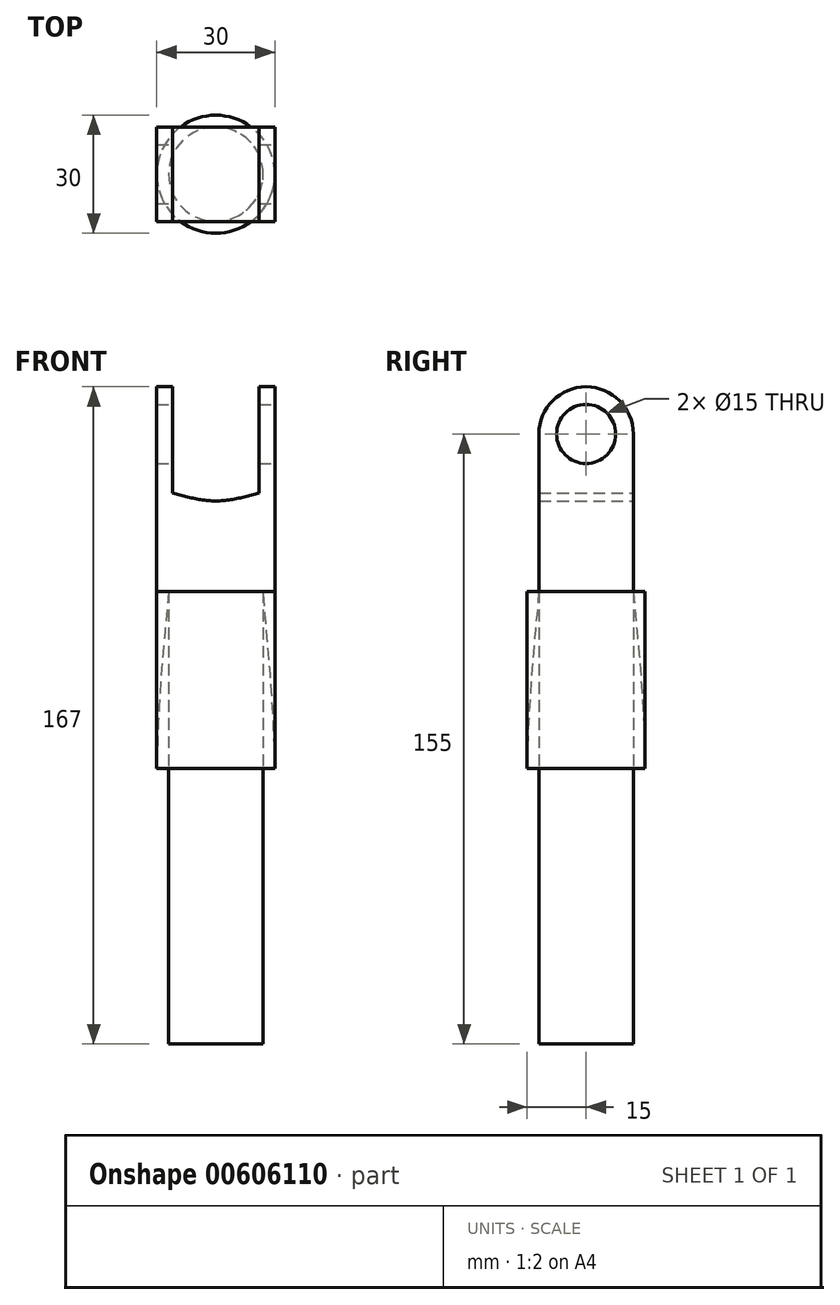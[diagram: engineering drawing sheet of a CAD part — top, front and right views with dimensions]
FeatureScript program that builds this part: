
annotation { "Feature Type Name" : "Feature", "Feature Type Description" : "" }
export const myFeature = defineFeature(function(context is Context, id is Id, definition is map)
    precondition{}
    {
        {
            var Q0;
            Q0=qCreatedBy(makeId("Top.planeOp"),FACE);
            var sketch = newSketch(context, id + "F0", { "sketchPlane" : qUnion([Q0])});
            skCircle(sketch, "E0", {"center": v(0, 0) * mm, "radius": 12 * mm});
            skSolve(sketch);
        }
        {
            var Q0;
            Q0=makeQuery(id+"F0.imprint","IMPRINT",FACE,{"disambiguationData":[TD([[makeQuery(id+"F0.imprint","IMPRINT",EDGE,{"derivedFrom":sQuery(id+"F0.wireOp",EDGE,"E0")}),1.0]])]});
            extrude(context, id + "F1", {"entities" : qUnion([Q0]), "endBound" : BoundingType.SYMMETRIC, "depth" : 30 * mm, "offsetDistance" : 25.4 * mm});
        }
        {
            var Q0;
            Q0=qCreatedBy(makeId("Right.planeOp"),FACE);
            var sketch = newSketch(context, id + "F2", { "sketchPlane" : qUnion([Q0])});
            skLineSegment(sketch, "E1.bottom", {"start": v(-15, 0) * mm, "end": v(15, 0) * mm});
            skLineSegment(sketch, "E1.top", {"start": v(-15, 100) * mm, "end": v(15, 100) * mm});
            skLineSegment(sketch, "E1.left", {"start": v(-15, 0) * mm, "end": v(-15, 100) * mm});
            skLineSegment(sketch, "E1.right", {"start": v(15, 0) * mm, "end": v(15, 100) * mm});
            skPoint(sketch, "E1.middle", {"position": v(0, 50) * mm});
            skLineSegment(sketch, "E2.bottom", {"start": v(-12, 100) * mm, "end": v(12, 100) * mm});
            skLineSegment(sketch, "E2.top", {"start": v(-12, 0) * mm, "end": v(12, 0) * mm});
            skLineSegment(sketch, "E2.left", {"start": v(-12, 100) * mm, "end": v(-12, 0) * mm});
            skLineSegment(sketch, "E2.right", {"start": v(12, 100) * mm, "end": v(12, 0) * mm});
            skFitSpline(sketch, "E3", {"points": [v(12, 100) * mm, v(15, 50) * mm, v(12, 15) * mm], "startDerivative": vector(8.76, -94.23) * mm, "endDerivative": vector(-9.56, -62.94) * mm});
            skLineSegment(sketch, "E4", {"start": v(0, 100) * mm, "end": v(0, 0) * mm, "construction": true});
            skLineSegment(sketch, "E5", {"start": v(12, 15) * mm, "end": v(0, 15) * mm});
            skLineSegment(sketch, "E6", {"start": v(0, 15) * mm, "end": v(0, 100) * mm});
            skSolve(sketch);
        }
        {
            var Q0;
            {var subQ5=sQuery(id+"F2.wireOp",EDGE,"E5");Q0=makeQuery(id+"F2.imprint","IMPRINT",FACE,{"disambiguationData":[TD([[makeQuery(id+"F2.imprint","IMPRINT",EDGE,{"derivedFrom":subQ5}),-1.0]])]});}
            var Q1;
            {var subQ0=sQuery(id+"F2.wireOp",EDGE,"E3");var subQ1=sQuery(id+"F2.wireOp",EDGE,"E1.right");var subQ2=makeQuery(id+"F2.imprint","INTERSECT",VERTEX,{"disambiguationData":[OD(0.0)],"derivedFrom":[subQ1,subQ0]});Q1=makeQuery(id+"F2.imprint","IMPRINT",FACE,{"disambiguationData":[TD([[makeQuery(id+"F2.imprint","IMPRINT",EDGE,{"disambiguationData":[TD([[subQ2,-1.0]])],"derivedFrom":subQ1}),1.0]])]});}
            var Q2;
            {var subQ0=sQuery(id+"F2.wireOp",EDGE,"E3");var subQ1=sQuery(id+"F2.wireOp",EDGE,"E1.right");var subQ2=makeQuery(id+"F2.imprint","INTERSECT",VERTEX,{"disambiguationData":[OD(0.0)],"derivedFrom":[subQ1,subQ0]});Q2=makeQuery(id+"F2.imprint","IMPRINT",FACE,{"disambiguationData":[TD([[makeQuery(id+"F2.imprint","IMPRINT",EDGE,{"disambiguationData":[TD([[subQ2,-1.0]])],"derivedFrom":subQ1}),-1.0]])]});}
            var Q3;
            Q3=sQuery(id+"F2.wireOp",EDGE,"E4");
            revolve(context, id + "F3", {"operationType" : NewBodyOperationType.ADD, "entities" : qUnion([Q0, Q1, Q2]), "axis" : qUnion([Q3]), "revolveType" : RevolveType.FULL});
        }
        {
            var Q0;
            Q0=qCreatedBy(makeId("Right.planeOp"),FACE);
            var sketch = newSketch(context, id + "F4", { "sketchPlane" : qUnion([Q0])});
            skLineSegment(sketch, "E7.bottom", {"start": v(12, 100) * mm, "end": v(-12, 100) * mm});
            skLineSegment(sketch, "E7.top", {"start": v(12, 140) * mm, "end": v(-12, 140) * mm});
            skLineSegment(sketch, "E7.left", {"start": v(12, 100) * mm, "end": v(12, 140) * mm});
            skLineSegment(sketch, "E7.right", {"start": v(-12, 100) * mm, "end": v(-12, 140) * mm});
            skPoint(sketch, "E7.middle", {"position": v(0, 120) * mm});
            skCircle(sketch, "E8", {"center": v(0, 140) * mm, "radius": 12 * mm});
            skCircle(sketch, "E9", {"center": v(0, 140) * mm, "radius": 7.5 * mm});
            skSolve(sketch);
        }
        {
            var Q0;
            Q0=makeQuery(id+"F4.imprint","IMPRINT",FACE,{"disambiguationData":[TD([[makeQuery(id+"F4.imprint","IMPRINT",EDGE,{"derivedFrom":sQuery(id+"F4.wireOp",EDGE,"E7.bottom")}),-1.0]])]});
            var Q1;
            {var subQ1=sQuery(id+"F4.wireOp",EDGE,"E7.top");var subQ3=sQuery(id+"F4.wireOp",EDGE,"E9");var subQ4=makeQuery(id+"F4.imprint","INTERSECT",VERTEX,{"disambiguationData":[OD(0.0)],"derivedFrom":[subQ1,subQ3]});Q1=makeQuery(id+"F4.imprint","IMPRINT",FACE,{"disambiguationData":[TD([[makeQuery(id+"F4.imprint","IMPRINT",EDGE,{"disambiguationData":[TD([[subQ4,1.0]])],"derivedFrom":subQ3}),-1.0]])]});}
            var Q2;
            {var subQ1=sQuery(id+"F4.wireOp",EDGE,"E7.top");var subQ3=sQuery(id+"F4.wireOp",EDGE,"E9");var subQ4=makeQuery(id+"F4.imprint","INTERSECT",VERTEX,{"disambiguationData":[OD(0.0)],"derivedFrom":[subQ1,subQ3]});Q2=makeQuery(id+"F4.imprint","IMPRINT",FACE,{"disambiguationData":[TD([[makeQuery(id+"F4.imprint","IMPRINT",EDGE,{"disambiguationData":[TD([[subQ4,-1.0]])],"derivedFrom":subQ3}),-1.0]])]});}
            extrude(context, id + "F5", {"entities" : qUnion([Q0, Q1, Q2]), "operationType" : NewBodyOperationType.ADD, "endBound" : BoundingType.SYMMETRIC, "oppositeDirection" : true, "depth" : 30 * mm, "offsetDistance" : 25.4 * mm});
        }
        {
            var Q0;
            Q0=makeQuery(id+"F5.opExtrude","SWEPT_FACE",FACE,{"disambiguationData":[OSD([sQuery(id+"F4.wireOp",EDGE,"E7.left")])]});
            var sketch = newSketch(context, id + "F6", { "sketchPlane" : qUnion([Q0])});
            skLineSegment(sketch, "E10.bottom", {"start": v(11, 155) * mm, "end": v(-11, 155) * mm});
            skLineSegment(sketch, "E10.top", {"start": v(11, 125) * mm, "end": v(-11, 125) * mm});
            skLineSegment(sketch, "E10.left", {"start": v(11, 155) * mm, "end": v(11, 125) * mm});
            skLineSegment(sketch, "E10.right", {"start": v(-11, 155) * mm, "end": v(-11, 125) * mm});
            skPoint(sketch, "E10.middle", {"position": v(0, 140) * mm});
            skLineSegment(sketch, "E11.bottom", {"start": v(11, 157) * mm, "end": v(-11, 157) * mm});
            skLineSegment(sketch, "E11.top", {"start": v(11, 123) * mm, "end": v(-11, 123) * mm});
            skLineSegment(sketch, "E11.left", {"start": v(11, 157) * mm, "end": v(11, 123) * mm});
            skLineSegment(sketch, "E11.right", {"start": v(-11, 157) * mm, "end": v(-11, 123) * mm});
            skFitSpline(sketch, "E12", {"points": [v(-11, 125) * mm, v(0, 123) * mm, v(11, 125) * mm], "startDerivative": vector(22, -6) * mm, "endDerivative": vector(22, 6) * mm});
            skSolve(sketch);
        }
        {
            var Q0;
            {var subQ0=sQuery(id+"F6.wireOp",EDGE,"E10.bottom");Q0=makeQuery(id+"F6.imprint","IMPRINT",FACE,{"disambiguationData":[TD([[makeQuery(id+"F6.imprint","IMPRINT",EDGE,{"derivedFrom":subQ0}),-1.0]])]});}
            var Q1;
            {var subQ0=sQuery(id+"F6.wireOp",EDGE,"E10.top");Q1=makeQuery(id+"F6.imprint","IMPRINT",FACE,{"disambiguationData":[TD([[makeQuery(id+"F6.imprint","IMPRINT",EDGE,{"derivedFrom":subQ0}),1.0]])]});}
            var Q2;
            {var subQ0=sQuery(id+"F6.wireOp",EDGE,"E10.bottom");Q2=makeQuery(id+"F6.imprint","IMPRINT",FACE,{"disambiguationData":[TD([[makeQuery(id+"F6.imprint","IMPRINT",EDGE,{"derivedFrom":subQ0}),1.0]])]});}
            var Q3;
            {var subQ0=sQuery(id+"F6.wireOp",EDGE,"E10.top");Q3=makeQuery(id+"F6.imprint","IMPRINT",FACE,{"disambiguationData":[TD([[makeQuery(id+"F6.imprint","IMPRINT",EDGE,{"derivedFrom":subQ0}),-1.0]])]});}
            extrude(context, id + "F7", {"entities" : qUnion([Q0, Q1, Q2, Q3]), "operationType" : NewBodyOperationType.REMOVE, "oppositeDirection" : true, "depth" : 25.4 * mm, "offsetDistance" : 25.4 * mm});
        }
    });
